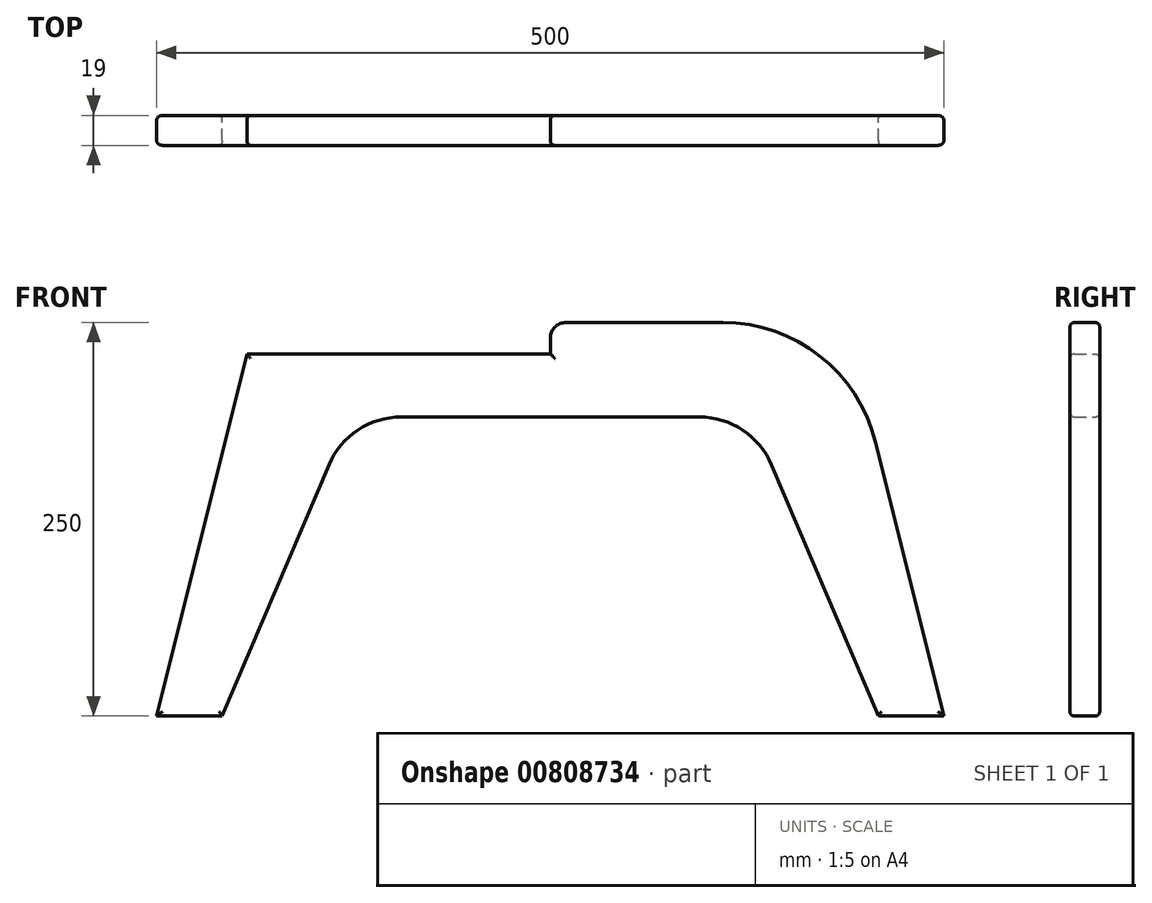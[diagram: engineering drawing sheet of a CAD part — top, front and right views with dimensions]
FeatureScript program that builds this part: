
annotation { "Feature Type Name" : "Feature", "Feature Type Description" : "" }
export const myFeature = defineFeature(function(context is Context, id is Id, definition is map)
    precondition{}
    {
        {
            var Q0;
            Q0=qCreatedBy(makeId("Front.planeOp"),FACE);
            var sketch = newSketch(context, id + "F0", { "sketchPlane" : qUnion([Q0])});
            skLineSegment(sketch, "E0", {"start": v(0, 0) * mm, "end": v(57.35, 230) * mm});
            skLineSegment(sketch, "E1", {"start": v(0, 0) * mm, "end": v(41.68, 0) * mm});
            skLineSegment(sketch, "E2", {"start": v(41.68, 0) * mm, "end": v(109.4, 159.54) * mm});
            skLineSegment(sketch, "E3", {"start": v(62.33, 250) * mm, "end": v(122.33, 190) * mm, "construction": true});
            skLineSegment(sketch, "E4", {"start": v(155.43, 190) * mm, "end": v(250, 190) * mm});
            skLineSegment(sketch, "E5", {"start": v(250, 240) * mm, "end": v(250, 230) * mm});
            skLineSegment(sketch, "E6.MirrorCS", {"start": v(359.54, 250) * mm, "end": v(260, 250) * mm});
            skLineSegment(sketch, "E7.MirrorCS", {"start": v(344.57, 190) * mm, "end": v(250, 190) * mm});
            skLineSegment(sketch, "E8.MirrorCS", {"start": v(458.32, 0) * mm, "end": v(390.6, 159.54) * mm});
            skLineSegment(sketch, "E9.MirrorCS", {"start": v(500, 0) * mm, "end": v(456.57, 174.2) * mm});
            skLineSegment(sketch, "E10.MirrorCS", {"start": v(500, 0) * mm, "end": v(458.32, 0) * mm});
            skPoint(sketch, "E11.visualSharp", {"position": v(437.67, 250) * mm});
            skArc(sketch, "E11.filletArc", {"start": v(456.57, 174.2) * mm, "mid": v(421.1, 228.8) * mm, "end": v(359.54, 250) * mm});
            skPoint(sketch, "E12.visualSharp", {"position": v(377.67, 190) * mm});
            skArc(sketch, "E12.filletArc", {"start": v(390.6, 159.54) * mm, "mid": v(372.17, 181.7) * mm, "end": v(344.57, 190) * mm});
            skLineSegment(sketch, "E13", {"start": v(250, 230) * mm, "end": v(57.35, 230) * mm});
            skPoint(sketch, "E14.visualSharp", {"position": v(122.33, 190) * mm});
            skArc(sketch, "E14.filletArc", {"start": v(155.43, 190) * mm, "mid": v(127.83, 181.7) * mm, "end": v(109.4, 159.54) * mm});
            skPoint(sketch, "E15.visualSharp", {"position": v(250, 250) * mm});
            skArc(sketch, "E15.filletArc", {"start": v(260, 250) * mm, "mid": v(252.93, 247.07) * mm, "end": v(250, 240) * mm});
            skSolve(sketch);
        }
        {
            var Q0;
            Q0=makeQuery(id+"F0.imprint","IMPRINT",FACE,{"disambiguationData":[TD([[makeQuery(id+"F0.imprint","IMPRINT",EDGE,{"derivedFrom":sQuery(id+"F0.wireOp",EDGE,"E0")}),-1.0]])]});
            extrude(context, id + "F1", {"entities" : qUnion([Q0]), "depth" : 19 * mm, "offsetDistance" : 25 * mm});
        }
        {
            var Q0;
            Q0=makeQuery(id+"F1.opExtrude","CAP_FACE",FACE,{"disambiguationData":[OSD([sQuery(id+"F0.wireOp",EDGE,"E0"),sQuery(id+"F0.wireOp",EDGE,"E1"),sQuery(id+"F0.wireOp",EDGE,"E2"),sQuery(id+"F0.wireOp",EDGE,"E4"),sQuery(id+"F0.wireOp",EDGE,"E5"),sQuery(id+"F0.wireOp",EDGE,"E6.MirrorCS"),sQuery(id+"F0.wireOp",EDGE,"E7.MirrorCS"),sQuery(id+"F0.wireOp",EDGE,"E8.MirrorCS"),sQuery(id+"F0.wireOp",EDGE,"E9.MirrorCS"),sQuery(id+"F0.wireOp",EDGE,"E10.MirrorCS"),sQuery(id+"F0.wireOp",EDGE,"E11.filletArc"),sQuery(id+"F0.wireOp",EDGE,"E12.filletArc"),sQuery(id+"F0.wireOp",EDGE,"E13"),sQuery(id+"F0.wireOp",EDGE,"E14.filletArc"),sQuery(id+"F0.wireOp",EDGE,"E15.filletArc")])],"isStart":false});
            var Q1;
            Q1=makeQuery(id+"F1.opExtrude","CAP_FACE",FACE,{"disambiguationData":[OSD([sQuery(id+"F0.wireOp",EDGE,"E0"),sQuery(id+"F0.wireOp",EDGE,"E1"),sQuery(id+"F0.wireOp",EDGE,"E2"),sQuery(id+"F0.wireOp",EDGE,"E4"),sQuery(id+"F0.wireOp",EDGE,"E5"),sQuery(id+"F0.wireOp",EDGE,"E6.MirrorCS"),sQuery(id+"F0.wireOp",EDGE,"E7.MirrorCS"),sQuery(id+"F0.wireOp",EDGE,"E8.MirrorCS"),sQuery(id+"F0.wireOp",EDGE,"E9.MirrorCS"),sQuery(id+"F0.wireOp",EDGE,"E10.MirrorCS"),sQuery(id+"F0.wireOp",EDGE,"E11.filletArc"),sQuery(id+"F0.wireOp",EDGE,"E12.filletArc"),sQuery(id+"F0.wireOp",EDGE,"E13"),sQuery(id+"F0.wireOp",EDGE,"E14.filletArc"),sQuery(id+"F0.wireOp",EDGE,"E15.filletArc")])],"isStart":true});
            fillet(context, id + "F2", {"entities" : qUnion([Q0, Q1]), "radius" : 3 * mm, "tangentPropagation" : true, "allowEdgeOverflow" : false});
        }
        {
            var Q0;
            Q0=makeQuery(id+"F1.opExtrude","SWEPT_FACE",FACE,{"disambiguationData":[OSD([sQuery(id+"F0.wireOp",EDGE,"E13")])]});
            var sketch = newSketch(context, id + "F3", { "sketchPlane" : qUnion([Q0])});
            skLineSegment(sketch, "E16", {"start": v(250, -9.5) * mm, "end": v(150, -9.5) * mm, "construction": true});
            skPoint(sketch, "E17", {"position": v(150, -9.5) * mm});
            skSolve(sketch);
        }
        {
            var Q0;
            Q0=makeQuery(id+"F1.opExtrude","CAP_FACE",FACE,{"disambiguationData":[OSD([sQuery(id+"F0.wireOp",EDGE,"E0"),sQuery(id+"F0.wireOp",EDGE,"E1"),sQuery(id+"F0.wireOp",EDGE,"E2"),sQuery(id+"F0.wireOp",EDGE,"E4"),sQuery(id+"F0.wireOp",EDGE,"E5"),sQuery(id+"F0.wireOp",EDGE,"E6.MirrorCS"),sQuery(id+"F0.wireOp",EDGE,"E7.MirrorCS"),sQuery(id+"F0.wireOp",EDGE,"E8.MirrorCS"),sQuery(id+"F0.wireOp",EDGE,"E9.MirrorCS"),sQuery(id+"F0.wireOp",EDGE,"E10.MirrorCS"),sQuery(id+"F0.wireOp",EDGE,"E11.filletArc"),sQuery(id+"F0.wireOp",EDGE,"E12.filletArc"),sQuery(id+"F0.wireOp",EDGE,"E13"),sQuery(id+"F0.wireOp",EDGE,"E14.filletArc"),sQuery(id+"F0.wireOp",EDGE,"E15.filletArc")])],"isStart":false});
            var sketch = newSketch(context, id + "F4", { "sketchPlane" : qUnion([Q0])});
            skPoint(sketch, "E18.0", {"position": v(59.69, 227) * mm});
            skPoint(sketch, "E19.0", {"position": v(453.66, 173.47) * mm});
            skLineSegment(sketch, "E20", {"start": v(453.66, 173.47) * mm, "end": v(443.96, 171.05) * mm, "construction": true});
            skLineSegment(sketch, "E21", {"start": v(443.96, 171.05) * mm, "end": v(451.21, 141.94) * mm, "construction": true});
            skPoint(sketch, "E22", {"position": v(451.21, 141.94) * mm});
            skLineSegment(sketch, "E23", {"start": v(59.69, 227) * mm, "end": v(52.43, 197.9) * mm, "construction": true});
            skLineSegment(sketch, "E24", {"start": v(52.43, 197.9) * mm, "end": v(62.13, 195.47) * mm, "construction": true});
            skPoint(sketch, "E25", {"position": v(62.13, 195.47) * mm});
            skSolve(sketch);
        }
        {
            var Q0;
            Q0=makeQuery(id+"F1.opExtrude","CAP_FACE",FACE,{"disambiguationData":[OSD([sQuery(id+"F0.wireOp",EDGE,"E0"),sQuery(id+"F0.wireOp",EDGE,"E1"),sQuery(id+"F0.wireOp",EDGE,"E2"),sQuery(id+"F0.wireOp",EDGE,"E4"),sQuery(id+"F0.wireOp",EDGE,"E5"),sQuery(id+"F0.wireOp",EDGE,"E6.MirrorCS"),sQuery(id+"F0.wireOp",EDGE,"E7.MirrorCS"),sQuery(id+"F0.wireOp",EDGE,"E8.MirrorCS"),sQuery(id+"F0.wireOp",EDGE,"E9.MirrorCS"),sQuery(id+"F0.wireOp",EDGE,"E10.MirrorCS"),sQuery(id+"F0.wireOp",EDGE,"E11.filletArc"),sQuery(id+"F0.wireOp",EDGE,"E12.filletArc"),sQuery(id+"F0.wireOp",EDGE,"E13"),sQuery(id+"F0.wireOp",EDGE,"E14.filletArc"),sQuery(id+"F0.wireOp",EDGE,"E15.filletArc")])],"isStart":true});
            var sketch = newSketch(context, id + "F5", { "sketchPlane" : qUnion([Q0])});
            skPoint(sketch, "E26.0", {"position": v(-62.13, 195.47) * mm});
            skPoint(sketch, "E27.0", {"position": v(-451.21, 141.94) * mm});
            skSolve(sketch);
        }
    });
